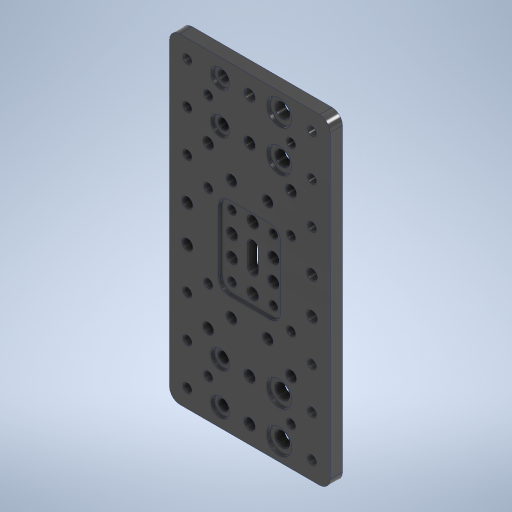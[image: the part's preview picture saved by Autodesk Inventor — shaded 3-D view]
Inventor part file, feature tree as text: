
AUTODESK INVENTOR PART (.ipt)
format: ipt  version: 2024.3 (Build 283343000, 343)  size: 385,536 bytes
history: native  units: in
note: dims shown in document units (in); Inventor stores cm internally (conversion verified against a paired STEP export)
features: mirror x1
ambient origin geometry x8: Origin, YZ Plane, XZ Plane, XY Plane, X Axis, Y Axis, Z Axis, Center Point
bodies: Solid1 (feature_tree)
feature tree (1):
  mirror  "Mirror1"
